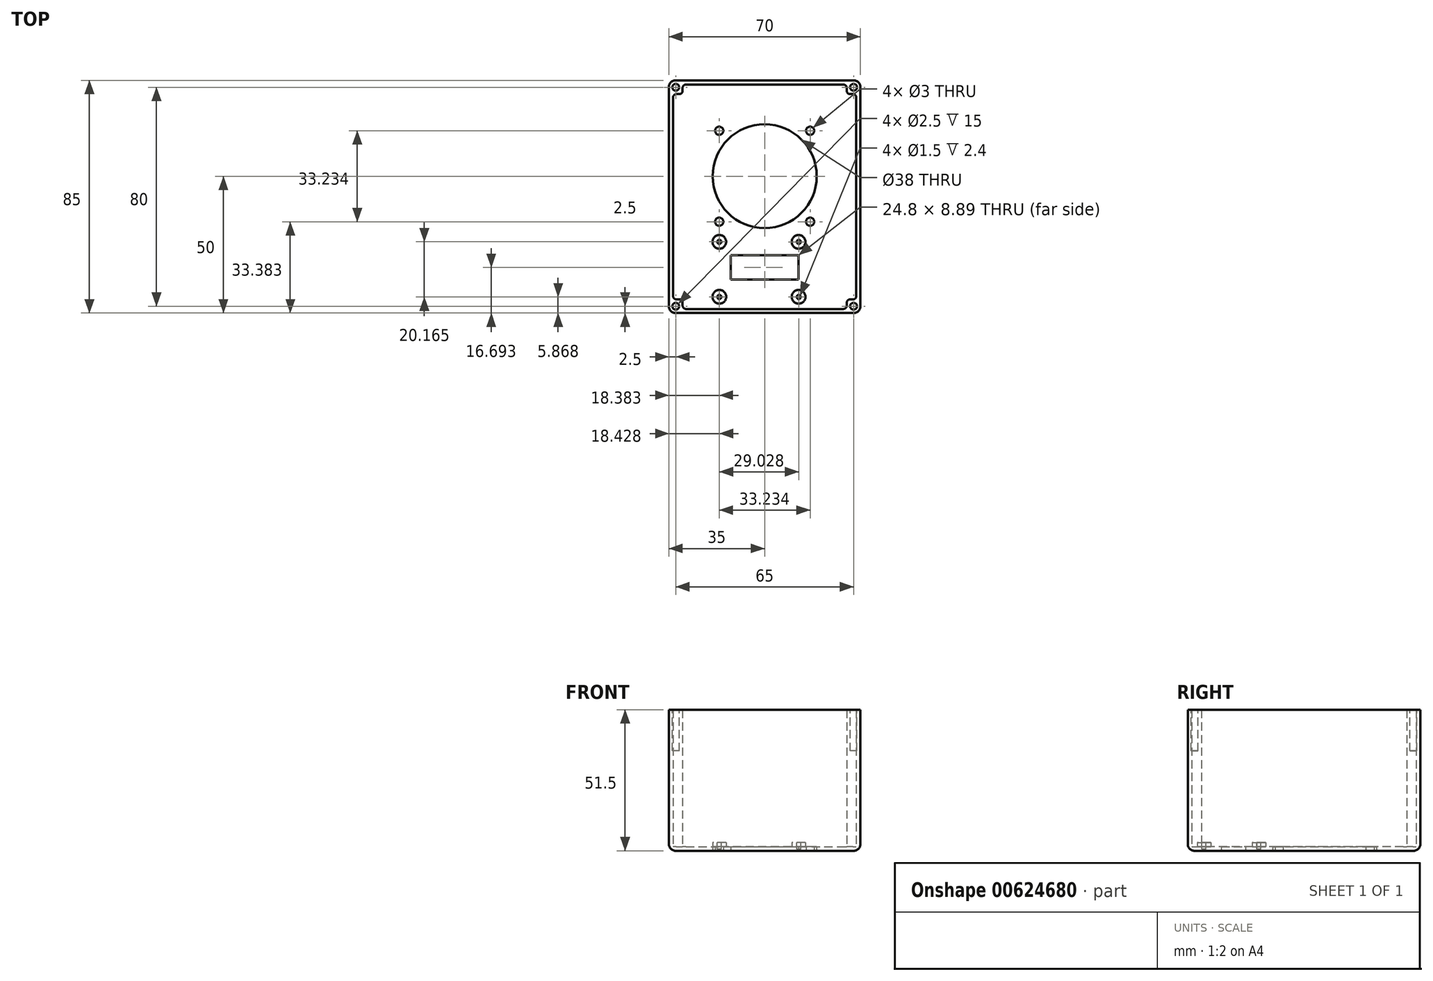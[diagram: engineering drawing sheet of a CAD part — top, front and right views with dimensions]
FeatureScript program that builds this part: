
annotation { "Feature Type Name" : "Feature", "Feature Type Description" : "" }
export const myFeature = defineFeature(function(context is Context, id is Id, definition is map)
    precondition{}
    {
        {
            var Q0;
            Q0=qCreatedBy(makeId("Top.planeOp"),FACE);
            var sketch = newSketch(context, id + "F0", { "sketchPlane" : qUnion([Q0])});
            skCircle(sketch, "E0", {"center": v(0, 0) * mm, "radius": 19 * mm});
            skCircle(sketch, "E1", {"center": v(0, 0) * mm, "radius": 23.5 * mm, "construction": true});
            skCircle(sketch, "E2", {"center": v(-16.62, 16.62) * mm, "radius": 1.5 * mm});
            skLineSegment(sketch, "E3", {"start": v(0, 0) * mm, "end": v(-16.62, 16.62) * mm, "construction": true});
            skCircle(sketch, "E4.1.0", {"center": v(-16.62, -16.62) * mm, "radius": 1.5 * mm});
            skCircle(sketch, "E4.2.0", {"center": v(16.62, -16.62) * mm, "radius": 1.5 * mm});
            skCircle(sketch, "E4.3.0", {"center": v(16.62, 16.62) * mm, "radius": 1.5 * mm});
            skCircle(sketch, "E5", {"center": v(-16.56, -24) * mm, "radius": 1.13 * mm, "construction": true});
            skCircle(sketch, "E6", {"center": v(12.4, -24) * mm, "radius": 1.13 * mm, "construction": true});
            skCircle(sketch, "E7", {"center": v(-16.56, -44.07) * mm, "radius": 1.13 * mm, "construction": true});
            skCircle(sketch, "E8", {"center": v(12.4, -44.07) * mm, "radius": 1.13 * mm, "construction": true});
            skLineSegment(sketch, "E9.bottom", {"start": v(-12.4, -37.75) * mm, "end": v(12.4, -37.75) * mm});
            skLineSegment(sketch, "E9.top", {"start": v(-12.4, -28.86) * mm, "end": v(12.4, -28.86) * mm});
            skLineSegment(sketch, "E9.left", {"start": v(-12.4, -37.75) * mm, "end": v(-12.4, -28.86) * mm});
            skLineSegment(sketch, "E9.right", {"start": v(12.4, -37.75) * mm, "end": v(12.4, -28.86) * mm});
            skLineSegment(sketch, "E10", {"start": v(-12.4, -28.86) * mm, "end": v(12.4, -37.75) * mm, "construction": true});
            skLineSegment(sketch, "E11", {"start": v(-12.4, -37.75) * mm, "end": v(12.4, -28.86) * mm, "construction": true});
            skLineSegment(sketch, "E12", {"start": v(0, -33.3) * mm, "end": v(0, -37.75) * mm, "construction": true});
            skLineSegment(sketch, "E13", {"start": v(0, 0) * mm, "end": v(0, -65.78) * mm, "construction": true});
            skLineSegment(sketch, "E14", {"start": v(0, -19) * mm, "end": v(-33.23, -19) * mm, "construction": true});
            skLineSegment(sketch, "E15.bottom", {"start": v(-35, -50) * mm, "end": v(35, -50) * mm});
            skLineSegment(sketch, "E15.top", {"start": v(-35, 35) * mm, "end": v(35, 35) * mm});
            skLineSegment(sketch, "E15.left", {"start": v(-35, -50) * mm, "end": v(-35, 35) * mm});
            skLineSegment(sketch, "E15.right", {"start": v(35, -50) * mm, "end": v(35, 35) * mm});
            skSolve(sketch);
        }
        {
            var Q0;
            Q0 = qSketchRegion(id + "F0", true);
            extrude(context, id + "F1", {"entities" : qUnion([Q0]), "depth" : 1.5 * mm, "offsetDistance" : 25 * mm});
        }
        {
            var Q0;
            Q0=makeQuery(id+"F1.opExtrude","CAP_FACE",FACE,{"disambiguationData":[OSD([sQuery(id+"F0.wireOp",EDGE,"E0"),sQuery(id+"F0.wireOp",EDGE,"E2"),sQuery(id+"F0.wireOp",EDGE,"E4.1.0"),sQuery(id+"F0.wireOp",EDGE,"E4.2.0"),sQuery(id+"F0.wireOp",EDGE,"E4.3.0"),sQuery(id+"F0.wireOp",EDGE,"E5"),sQuery(id+"F0.wireOp",EDGE,"E6"),sQuery(id+"F0.wireOp",EDGE,"E7"),sQuery(id+"F0.wireOp",EDGE,"E8"),sQuery(id+"F0.wireOp",EDGE,"E9.bottom"),sQuery(id+"F0.wireOp",EDGE,"E9.top"),sQuery(id+"F0.wireOp",EDGE,"E9.left"),sQuery(id+"F0.wireOp",EDGE,"E9.right"),sQuery(id+"F0.wireOp",EDGE,"E15.bottom"),sQuery(id+"F0.wireOp",EDGE,"E15.top"),sQuery(id+"F0.wireOp",EDGE,"E15.left"),sQuery(id+"F0.wireOp",EDGE,"E15.right")])],"isStart":false});
            var sketch = newSketch(context, id + "F2", { "sketchPlane" : qUnion([Q0])});
            skLineSegment(sketch, "E16.bottom", {"start": v(-35, 35) * mm, "end": v(35, 35) * mm});
            skLineSegment(sketch, "E16.top", {"start": v(-35, -50) * mm, "end": v(35, -50) * mm});
            skLineSegment(sketch, "E16.left", {"start": v(-35, 35) * mm, "end": v(-35, -50) * mm});
            skLineSegment(sketch, "E16.right", {"start": v(35, 35) * mm, "end": v(35, -50) * mm});
            skLineSegment(sketch, "E17.bottom", {"start": v(-30, 33.5) * mm, "end": v(30, 33.5) * mm});
            skLineSegment(sketch, "E17.top", {"start": v(-30, -48.5) * mm, "end": v(30, -48.5) * mm});
            skLineSegment(sketch, "E17.left", {"start": v(-33.5, 30) * mm, "end": v(-33.5, -45) * mm});
            skLineSegment(sketch, "E17.right", {"start": v(33.5, 30) * mm, "end": v(33.5, -45) * mm});
            skLineSegment(sketch, "E18.top", {"start": v(-33.5, 30) * mm, "end": v(-30, 30) * mm});
            skLineSegment(sketch, "E18.right", {"start": v(-30, 33.5) * mm, "end": v(-30, 30) * mm});
            skLineSegment(sketch, "E19.top", {"start": v(33.5, 30) * mm, "end": v(30, 30) * mm});
            skLineSegment(sketch, "E19.right", {"start": v(30, 33.5) * mm, "end": v(30, 30) * mm});
            skLineSegment(sketch, "E20.top", {"start": v(-33.5, -45) * mm, "end": v(-30, -45) * mm});
            skLineSegment(sketch, "E20.right", {"start": v(-30, -48.5) * mm, "end": v(-30, -45) * mm});
            skLineSegment(sketch, "E21.top", {"start": v(33.5, -45) * mm, "end": v(30, -45) * mm});
            skLineSegment(sketch, "E21.right", {"start": v(30, -48.5) * mm, "end": v(30, -45) * mm});
            skSolve(sketch);
        }
        {
            var Q0;
            Q0 = qSketchRegion(id + "F2", true);
            extrude(context, id + "F3", {"entities" : qUnion([Q0]), "operationType" : NewBodyOperationType.ADD, "depth" : 50 * mm, "offsetDistance" : 25 * mm});
        }
        {
            var Q0;
            Q0=makeQuery(id+"F3.opExtrude","CAP_FACE",FACE,{"disambiguationData":[OSD([sQuery(id+"F2.wireOp",EDGE,"E16.bottom"),sQuery(id+"F2.wireOp",EDGE,"E16.top"),sQuery(id+"F2.wireOp",EDGE,"E16.left"),sQuery(id+"F2.wireOp",EDGE,"E16.right"),sQuery(id+"F2.wireOp",EDGE,"E17.bottom"),sQuery(id+"F2.wireOp",EDGE,"E17.top"),sQuery(id+"F2.wireOp",EDGE,"E17.left"),sQuery(id+"F2.wireOp",EDGE,"E17.right"),sQuery(id+"F2.wireOp",EDGE,"E18.top"),sQuery(id+"F2.wireOp",EDGE,"E18.right"),sQuery(id+"F2.wireOp",EDGE,"E19.top"),sQuery(id+"F2.wireOp",EDGE,"E19.right"),sQuery(id+"F2.wireOp",EDGE,"E20.top"),sQuery(id+"F2.wireOp",EDGE,"E20.right"),sQuery(id+"F2.wireOp",EDGE,"E21.top"),sQuery(id+"F2.wireOp",EDGE,"E21.right")])],"isStart":false});
            var sketch = newSketch(context, id + "F4", { "sketchPlane" : qUnion([Q0])});
            skCircle(sketch, "E22", {"center": v(-32.5, 32.5) * mm, "radius": 1.25 * mm});
            skCircle(sketch, "E23", {"center": v(32.5, -47.5) * mm, "radius": 1.25 * mm});
            skCircle(sketch, "E24", {"center": v(32.5, 32.5) * mm, "radius": 1.25 * mm});
            skCircle(sketch, "E25", {"center": v(-32.5, -47.5) * mm, "radius": 1.25 * mm});
            skSolve(sketch);
        }
        {
            var Q0;
            Q0 = qSketchRegion(id + "F4", true);
            extrude(context, id + "F5", {"entities" : qUnion([Q0]), "operationType" : NewBodyOperationType.REMOVE, "oppositeDirection" : true, "depth" : 15 * mm, "offsetDistance" : 25 * mm});
        }
        {
            var Q0;
            Q0=makeQuery(id+"F0.imprint","IMPRINT",FACE,{"disambiguationData":[TD([[makeQuery(id+"F0.imprint","IMPRINT",EDGE,{"derivedFrom":sQuery(id+"F0.wireOp",EDGE,"E0")}),-1.0]])]});
            var sketch = newSketch(context, id + "F6", { "sketchPlane" : qUnion([Q0])});
            skCircle(sketch, "E26", {"center": v(-16.57, -23.97) * mm, "radius": 2.5 * mm});
            skCircle(sketch, "E27", {"center": v(12.4, -24) * mm, "radius": 2.5 * mm});
            skCircle(sketch, "E28", {"center": v(12.4, -44.07) * mm, "radius": 2.5 * mm});
            skCircle(sketch, "E29", {"center": v(-16.56, -44.06) * mm, "radius": 2.5 * mm});
            skSolve(sketch);
        }
        {
            var Q0;
            Q0 = qSketchRegion(id + "F6", true);
            extrude(context, id + "F7", {"entities" : qUnion([Q0]), "operationType" : NewBodyOperationType.ADD, "depth" : 3 * mm, "offsetDistance" : 25 * mm});
        }
        {
            var Q0;
            Q0=makeQuery(id+"F7.opExtrude","CAP_FACE",FACE,{"disambiguationData":[OSD([sQuery(id+"F6.wireOp",EDGE,"E26")])],"isStart":false});
            var sketch = newSketch(context, id + "F8", { "sketchPlane" : qUnion([Q0])});
            skCircle(sketch, "E30", {"center": v(-16.57, -23.97) * mm, "radius": 0.75 * mm});
            skCircle(sketch, "E31", {"center": v(12.46, -24) * mm, "radius": 0.75 * mm});
            skCircle(sketch, "E32", {"center": v(12.46, -44.13) * mm, "radius": 0.75 * mm});
            skCircle(sketch, "E33", {"center": v(-16.57, -44.13) * mm, "radius": 0.75 * mm});
            skSolve(sketch);
        }
        {
            var Q0;
            Q0 = qSketchRegion(id + "F8", true);
            extrude(context, id + "F9", {"entities" : qUnion([Q0]), "operationType" : NewBodyOperationType.REMOVE, "oppositeDirection" : true, "depth" : 2.4 * mm, "offsetDistance" : 25 * mm});
        }
        {
            var Q0;
            Q0=makeQuery(id+"F3.boolean.opBoolean","MERGE",EDGE,{"derivedFrom":[makeQuery(id+"F1.opExtrude","SWEPT_EDGE",EDGE,{"disambiguationData":[OSD([sQuery(id+"F0.wireOp",EDGE,"E15.top"),sQuery(id+"F0.wireOp",EDGE,"E15.left")])]}),makeQuery(id+"F3.opExtrude","SWEPT_EDGE",EDGE,{"disambiguationData":[OSD([sQuery(id+"F2.wireOp",EDGE,"E16.bottom"),sQuery(id+"F2.wireOp",EDGE,"E16.left")])]})]});
            var Q1;
            Q1=makeQuery(id+"F3.boolean.opBoolean","MERGE",EDGE,{"derivedFrom":[makeQuery(id+"F1.opExtrude","SWEPT_EDGE",EDGE,{"disambiguationData":[OSD([sQuery(id+"F0.wireOp",EDGE,"E15.bottom"),sQuery(id+"F0.wireOp",EDGE,"E15.left")])]}),makeQuery(id+"F3.opExtrude","SWEPT_EDGE",EDGE,{"disambiguationData":[OSD([sQuery(id+"F2.wireOp",EDGE,"E16.top"),sQuery(id+"F2.wireOp",EDGE,"E16.left")])]})]});
            var Q2;
            Q2=makeQuery(id+"F1.opExtrude","CAP_EDGE",EDGE,{"disambiguationData":[OSD([sQuery(id+"F0.wireOp",EDGE,"E15.left")])],"isStart":true});
            var Q3;
            Q3=makeQuery(id+"F1.opExtrude","CAP_EDGE",EDGE,{"disambiguationData":[OSD([sQuery(id+"F0.wireOp",EDGE,"E15.top")])],"isStart":true});
            var Q4;
            Q4=makeQuery(id+"F1.opExtrude","CAP_EDGE",EDGE,{"disambiguationData":[OSD([sQuery(id+"F0.wireOp",EDGE,"E15.right")])],"isStart":true});
            var Q5;
            Q5=makeQuery(id+"F1.opExtrude","CAP_EDGE",EDGE,{"disambiguationData":[OSD([sQuery(id+"F0.wireOp",EDGE,"E15.bottom")])],"isStart":true});
            var Q6;
            Q6=makeQuery(id+"F3.boolean.opBoolean","MERGE",EDGE,{"derivedFrom":[makeQuery(id+"F1.opExtrude","SWEPT_EDGE",EDGE,{"disambiguationData":[OSD([sQuery(id+"F0.wireOp",EDGE,"E15.top"),sQuery(id+"F0.wireOp",EDGE,"E15.right")])]}),makeQuery(id+"F3.opExtrude","SWEPT_EDGE",EDGE,{"disambiguationData":[OSD([sQuery(id+"F2.wireOp",EDGE,"E16.bottom"),sQuery(id+"F2.wireOp",EDGE,"E16.right")])]})]});
            var Q7;
            Q7=makeQuery(id+"F3.boolean.opBoolean","MERGE",EDGE,{"derivedFrom":[makeQuery(id+"F1.opExtrude","SWEPT_EDGE",EDGE,{"disambiguationData":[OSD([sQuery(id+"F0.wireOp",EDGE,"E15.bottom"),sQuery(id+"F0.wireOp",EDGE,"E15.right")])]}),makeQuery(id+"F3.opExtrude","SWEPT_EDGE",EDGE,{"disambiguationData":[OSD([sQuery(id+"F2.wireOp",EDGE,"E16.top"),sQuery(id+"F2.wireOp",EDGE,"E16.right")])]})]});
            fillet(context, id + "F10", {"entities" : qUnion([Q0, Q1, Q2, Q3, Q4, Q5, Q6, Q7]), "radius" : 2.4 * mm, "tangentPropagation" : true, "allowEdgeOverflow" : false});
        }
        {
            var Q0;
            Q0=makeQuery(id+"F3.opExtrude","CAP_EDGE",EDGE,{"disambiguationData":[OSD([sQuery(id+"F2.wireOp",EDGE,"E17.bottom")])],"isStart":true});
            var Q1;
            Q1=makeQuery(id+"F3.opExtrude","CAP_EDGE",EDGE,{"disambiguationData":[OSD([sQuery(id+"F2.wireOp",EDGE,"E18.right")])],"isStart":true});
            var Q2;
            Q2=makeQuery(id+"F3.opExtrude","CAP_EDGE",EDGE,{"disambiguationData":[OSD([sQuery(id+"F2.wireOp",EDGE,"E18.top")])],"isStart":true});
            var Q3;
            Q3=makeQuery(id+"F3.opExtrude","SWEPT_EDGE",EDGE,{"disambiguationData":[OSD([sQuery(id+"F2.wireOp",EDGE,"E18.top"),sQuery(id+"F2.wireOp",EDGE,"E18.right")])]});
            var Q4;
            Q4=makeQuery(id+"F3.opExtrude","SWEPT_EDGE",EDGE,{"disambiguationData":[OSD([sQuery(id+"F2.wireOp",EDGE,"E17.bottom"),sQuery(id+"F2.wireOp",EDGE,"E18.right")])]});
            var Q5;
            Q5=makeQuery(id+"F3.opExtrude","SWEPT_EDGE",EDGE,{"disambiguationData":[OSD([sQuery(id+"F2.wireOp",EDGE,"E17.left"),sQuery(id+"F2.wireOp",EDGE,"E18.top")])]});
            var Q6;
            Q6=makeQuery(id+"F3.opExtrude","CAP_EDGE",EDGE,{"disambiguationData":[OSD([sQuery(id+"F2.wireOp",EDGE,"E17.left")])],"isStart":true});
            var Q7;
            Q7=makeQuery(id+"F3.opExtrude","CAP_EDGE",EDGE,{"disambiguationData":[OSD([sQuery(id+"F2.wireOp",EDGE,"E19.right")])],"isStart":true});
            var Q8;
            Q8=makeQuery(id+"F3.opExtrude","CAP_EDGE",EDGE,{"disambiguationData":[OSD([sQuery(id+"F2.wireOp",EDGE,"E19.top")])],"isStart":true});
            var Q9;
            Q9=makeQuery(id+"F3.opExtrude","SWEPT_EDGE",EDGE,{"disambiguationData":[OSD([sQuery(id+"F2.wireOp",EDGE,"E19.top"),sQuery(id+"F2.wireOp",EDGE,"E19.right")])]});
            var Q10;
            Q10=makeQuery(id+"F3.opExtrude","SWEPT_EDGE",EDGE,{"disambiguationData":[OSD([sQuery(id+"F2.wireOp",EDGE,"E17.bottom"),sQuery(id+"F2.wireOp",EDGE,"E19.right")])]});
            var Q11;
            Q11=makeQuery(id+"F3.opExtrude","SWEPT_EDGE",EDGE,{"disambiguationData":[OSD([sQuery(id+"F2.wireOp",EDGE,"E17.right"),sQuery(id+"F2.wireOp",EDGE,"E19.top")])]});
            var Q12;
            Q12=makeQuery(id+"F3.opExtrude","CAP_EDGE",EDGE,{"disambiguationData":[OSD([sQuery(id+"F2.wireOp",EDGE,"E17.right")])],"isStart":true});
            var Q13;
            Q13=makeQuery(id+"F3.opExtrude","SWEPT_EDGE",EDGE,{"disambiguationData":[OSD([sQuery(id+"F2.wireOp",EDGE,"E17.left"),sQuery(id+"F2.wireOp",EDGE,"E20.top")])]});
            var Q14;
            Q14=makeQuery(id+"F3.opExtrude","SWEPT_EDGE",EDGE,{"disambiguationData":[OSD([sQuery(id+"F2.wireOp",EDGE,"E20.top"),sQuery(id+"F2.wireOp",EDGE,"E20.right")])]});
            var Q15;
            Q15=makeQuery(id+"F3.opExtrude","CAP_EDGE",EDGE,{"disambiguationData":[OSD([sQuery(id+"F2.wireOp",EDGE,"E20.top")])],"isStart":true});
            var Q16;
            Q16=makeQuery(id+"F3.opExtrude","SWEPT_EDGE",EDGE,{"disambiguationData":[OSD([sQuery(id+"F2.wireOp",EDGE,"E17.top"),sQuery(id+"F2.wireOp",EDGE,"E20.right")])]});
            var Q17;
            Q17=makeQuery(id+"F3.opExtrude","CAP_EDGE",EDGE,{"disambiguationData":[OSD([sQuery(id+"F2.wireOp",EDGE,"E17.top")])],"isStart":true});
            var Q18;
            Q18=makeQuery(id+"F3.opExtrude","CAP_EDGE",EDGE,{"disambiguationData":[OSD([sQuery(id+"F2.wireOp",EDGE,"E21.right")])],"isStart":true});
            var Q19;
            Q19=makeQuery(id+"F3.opExtrude","CAP_EDGE",EDGE,{"disambiguationData":[OSD([sQuery(id+"F2.wireOp",EDGE,"E21.top")])],"isStart":true});
            var Q20;
            Q20=makeQuery(id+"F3.opExtrude","SWEPT_EDGE",EDGE,{"disambiguationData":[OSD([sQuery(id+"F2.wireOp",EDGE,"E21.top"),sQuery(id+"F2.wireOp",EDGE,"E21.right")])]});
            var Q21;
            Q21=makeQuery(id+"F3.opExtrude","SWEPT_EDGE",EDGE,{"disambiguationData":[OSD([sQuery(id+"F2.wireOp",EDGE,"E17.right"),sQuery(id+"F2.wireOp",EDGE,"E21.top")])]});
            var Q22;
            Q22=makeQuery(id+"F3.opExtrude","SWEPT_EDGE",EDGE,{"disambiguationData":[OSD([sQuery(id+"F2.wireOp",EDGE,"E17.top"),sQuery(id+"F2.wireOp",EDGE,"E21.right")])]});
            fillet(context, id + "F11", {"entities" : qUnion([Q0, Q1, Q2, Q3, Q4, Q5, Q6, Q7, Q8, Q9, Q10, Q11, Q12, Q13, Q14, Q15, Q16, Q17, Q18, Q19, Q20, Q21, Q22]), "radius" : 1.2 * mm, "tangentPropagation" : true, "allowEdgeOverflow" : false});
        }
    });
